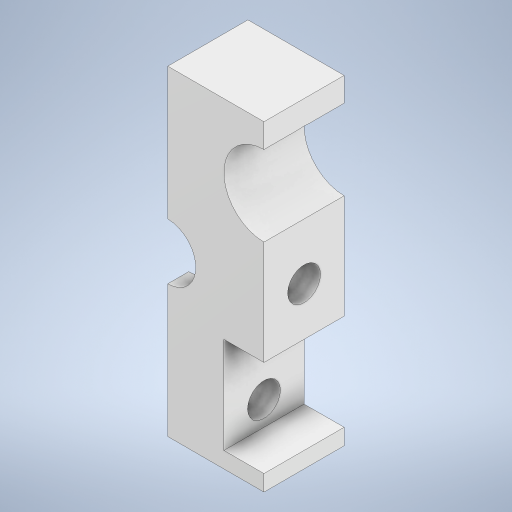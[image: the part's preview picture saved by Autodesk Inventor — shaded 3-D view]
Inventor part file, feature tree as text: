
AUTODESK INVENTOR PART (.ipt)
format: ipt  version: 2023 (Build 270158000, 158)  size: 317,952 bytes
history: native  units: mm
features: extrude x7, sketch x7, plane x1
ambient origin geometry x8: Origin, YZ Plane, XZ Plane, XY Plane, X Axis, Y Axis, Z Axis, Center Point
bodies: Solid1 (feature_tree)
feature tree (15):
  extrude  "Extrusion1"  Depth=20.0mm
  plane  "Work Plane1"
  extrude  "Extrusion2"  Depth=2.0mm
  extrude  "Extrusion3"  Depth=4.0mm
  extrude  "Extrusion4"  Depth=5.0mm TaperAngle=0.0deg
  extrude  "Extrusion5"  Depth=2.4mm TaperAngle=0.0deg
  extrude  "Extrusion6"  Depth=8.0mm TaperAngle=0.0deg
  extrude  "Extrusion7"  Depth=10.0mm
  sketch  "Sketch1"  dims[d0=20.0mm d1=20.0mm]
  sketch  "Sketch2"  dims[d2=4.0mm d6=2.0mm]
  sketch  "Sketch3"  dims[d7=2.0mm d8=4.0mm]
  sketch  "Sketch4"  dims[d9=2.0mm d10=5.0mm d11=0.0mm]
  sketch  "Sketch5"  dims[d12=5.5mm d13=2.4mm d14=0.0mm]
  sketch  "Sketch6"  dims[d15=3.5mm d16=8.0mm d17=0.0mm]
  sketch  "Sketch7"  dims[d18=2.05mm d19=2.05mm d20=2.5mm d21=2.5mm d22=2.5mm d23=2.5mm d24=25.0mm d25=0.0mm d30=5.0mm d31=0.0mm d32=2.5mm d33=1.0mm d34=6.0mm d35=5.0mm d36=4.0mm d37=5.0mm d38=0.0mm d39=2.5mm d40=10.0mm d41=2.05mm d42=20.0mm d43=0.0mm]
